# Revit family: ROTADO_ПереходныеЭлементы_ПлоскоеОснование
name_source: partatom
category: Арматура воздуховодов
units: mm (PartAtom-declared; Revit-internal decimal feet)

## family parameters
Всегда вертикально = Да
На основе рабочей плоскости = Нет
Общий = Нет
При загрузке вырезать с полостями = Нет
Размер круглого соединителя = Использовать диаметр
Тип детали = Присоединяется

## types (7) — shared parameters
ADSK_URL документации изделия = https://rotado.ru
ADSK_URL страницы изделия = https://rotado.ru
ADSK_Версия Revit = 2019
ADSK_Единица измерения = шт.
ADSK_Завод-изготовитель = ROTADO
ADSK_Количество = 1
ADSK_Материал = ROTADO_Сталь_Нержавеющая_Оцинкованная
ADSK_Наименование = Плоское основание
URL = https://rotado.ru
Изготовитель = ROTADO
Производитель_Контакты_Телефон = 88007002460

## per-type parameters (varying)
| type | ADSK_Марка | ADSK_Масса | ADSK_Масса_Текст | ADSK_Обозначение | ADSK_Размер_Высота | ADSK_Размер_Диаметр | ADSK_Размер_Длина | ADSK_Размер_Ширина | C | D | D_1 | H |
| TST-315 | TST-315 | 3 | 3 | TST-315 | 250 мм | 315 мм | 390 мм | 390 мм | 390 мм | 315 мм | 316 мм | 250 мм |
| TST-355 | TST-315 | 3.2 | 3.2 | TST-315 | 250 мм | 355 мм | 490 мм | 490 мм | 490 мм | 355 мм | 356 мм | 250 мм |
| TST-400 | TST-400 | 4 | 4 | TST-400 | 300 мм | 400 мм | 490 мм | 490 мм | 490 мм | 400 мм | 401 мм | 300 мм |
| TST-500 | TST-500 | 5 | 5 | TST-500 | 310 мм | 500 мм | 615 мм | 615 мм | 615 мм | 500 мм | 501 мм | 310 мм |
| TST-600 | TST-600 | 7 | 7 | TST-600 | 320 мм | 600 мм | 800 мм | 800 мм | 800 мм | 600 мм | 601 мм | 320 мм |
| TST-680 | TST-680 | 9 | 9 | TST-680 | 350 мм | 680 мм | 880 мм | 880 мм | 880 мм | 680 мм | 681 мм | 350 мм |
| TST-800 | TST-800 | 11 | 11 | TST-800 | 400 мм | 800 мм | 1000 мм | 1000 мм | 1000 мм | 800 мм | 801 мм | 400 мм |
